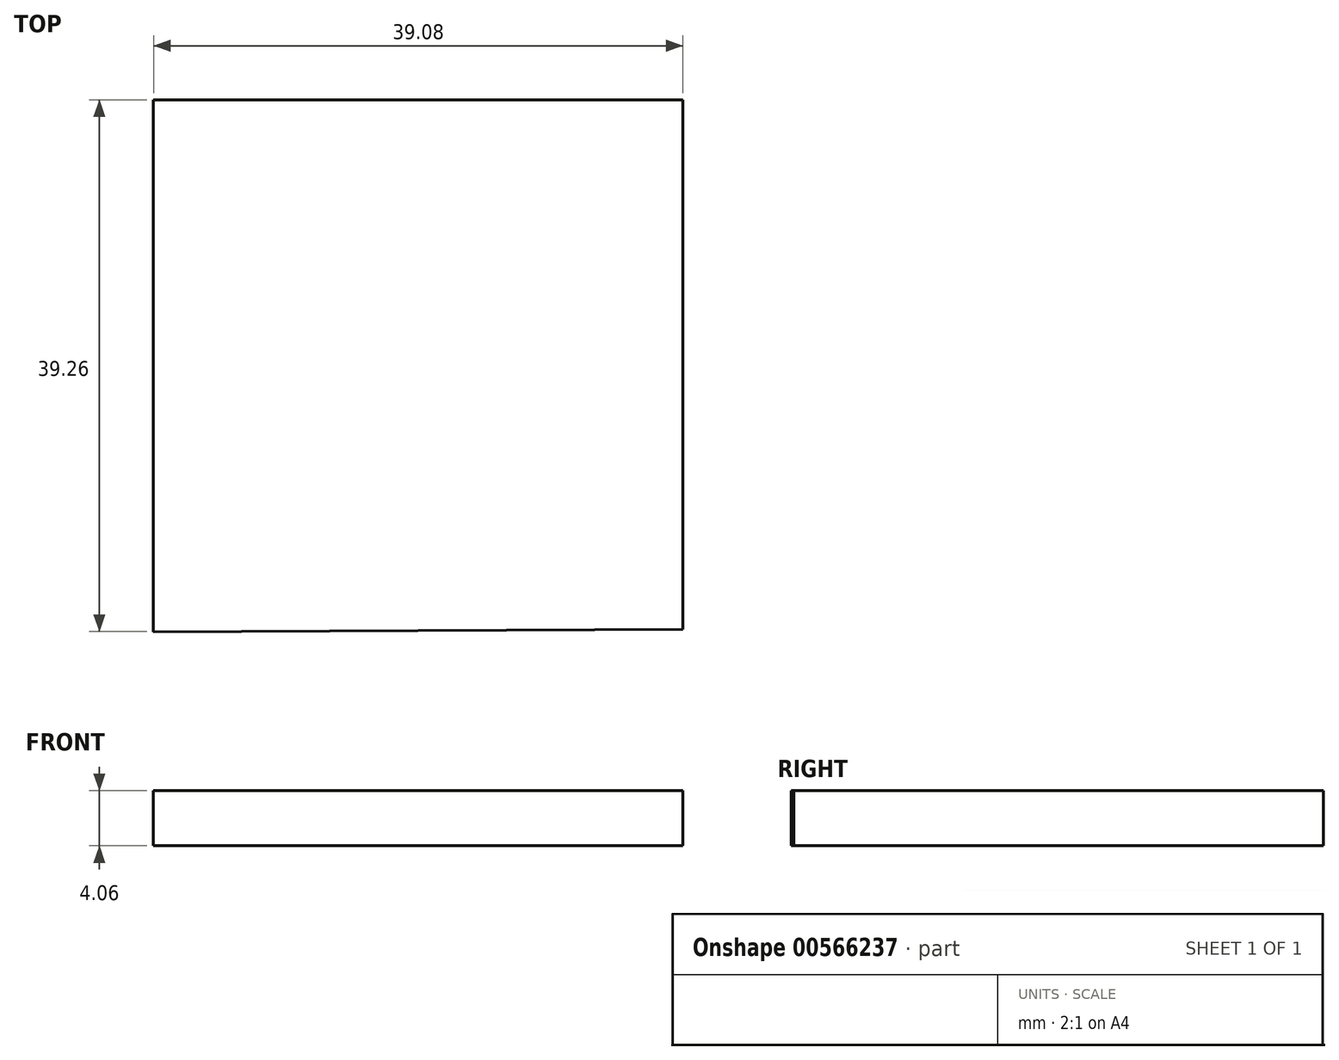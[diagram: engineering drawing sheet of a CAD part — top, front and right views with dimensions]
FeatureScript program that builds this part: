
annotation { "Feature Type Name" : "Feature", "Feature Type Description" : "" }
export const myFeature = defineFeature(function(context is Context, id is Id, definition is map)
    precondition{}
    {
        {
            var Q0;
            Q0=qCreatedBy(makeId("Top.planeOp"),FACE);
            var sketch = newSketch(context, id + "F0", { "sketchPlane" : qUnion([Q0])});
            skLineSegment(sketch, "E0", {"start": v(-39.08, -11.61) * mm, "end": v(-39.08, 27.65) * mm});
            skLineSegment(sketch, "E1", {"start": v(0, 27.65) * mm, "end": v(0, -11.43) * mm});
            skLineSegment(sketch, "E2", {"start": v(0, -11.43) * mm, "end": v(-39.08, -11.61) * mm});
            skLineSegment(sketch, "E3", {"start": v(-39.08, 27.65) * mm, "end": v(0, 27.65) * mm});
            skSolve(sketch);
        }
        {
            var Q0;
            Q0=makeQuery(id+"F0.imprint","IMPRINT",FACE,{"disambiguationData":[TD([[makeQuery(id+"F0.imprint","IMPRINT",EDGE,{"derivedFrom":sQuery(id+"F0.wireOp",EDGE,"E0")}),-1.0]])]});
            extrude(context, id + "F1", {"entities" : qUnion([Q0]), "depth" : 4.06 * mm, "offsetDistance" : 25.4 * mm});
        }
    });
